AUTODESK INVENTOR PART (.ipt)
format: ipt  version: 2021 (Build 250183000, 183)  size: 3,831,808 bytes
history: native  units: mm
features: other x15, sketch x2, extrude x1, projected_geometry x1, surface_op x1
ambient origin geometry x8: Origin, YZ Plane, XZ Plane, XY Plane, X Axis, Y Axis, Z Axis, Center Point
bodies: Body1 (feature_tree)
feature tree (20):
  other  "Sólido1"
  other  "leonOSM"
  other  "SCU1"
  extrude  "Extrusión1"  Depth=1700000.0mm
  sketch  "Boceto3"  dims[d9=2000000.0mm d10=1000.0mm d11=0.0mm d12=1000000.0mm d13=850000.0mm d14=1500000.0mm d15=2000000.0mm d16=1500000.0mm]
  sketch  "Boceto1"  dims[d0=0.0mm d1=0.0mm d2=0.0mm d3=0.0mm d4=0.0mm d5=0.0mm d7=1700000.0mm]
  projected_geometry  "Contorno proyectado1"
  other  "BuildingEntrance"
  other  "Building"
  other  "Pool"
  other  "SoccerPitch"
  other  "RoadArea"
  surface_op  "SurfaceArea"
  other  "SCU1: Plano YZ"
  other  "SCU1: Plano XZ"
  other  "SCU1: Plano XY"
  other  "SCU1: Eje X"
  other  "SCU1: Eje Y"
  other  "SCU1: Eje Z"
  other  "SCU1: Centro"
